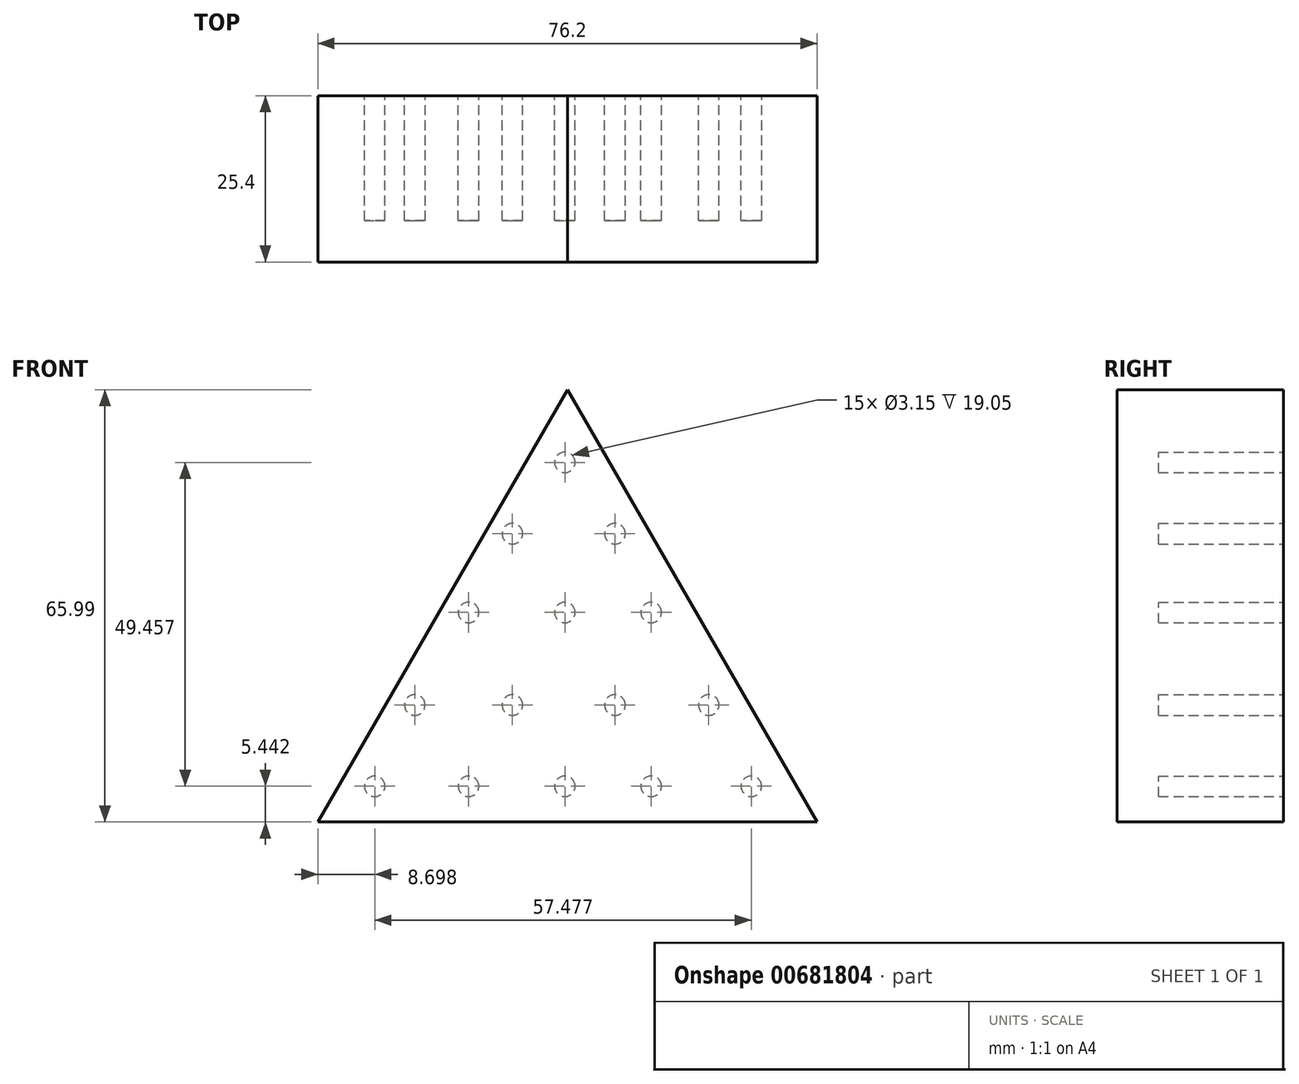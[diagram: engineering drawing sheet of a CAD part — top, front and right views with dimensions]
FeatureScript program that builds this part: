
annotation { "Feature Type Name" : "Feature", "Feature Type Description" : "" }
export const myFeature = defineFeature(function(context is Context, id is Id, definition is map)
    precondition{}
    {
        {
            var Q0;
            Q0=qCreatedBy(makeId("Front.planeOp"),FACE);
            var sketch = newSketch(context, id + "F0", { "sketchPlane" : qUnion([Q0])});
            skLineSegment(sketch, "E0", {"start": v(0, 0) * mm, "end": v(-38.1, 66) * mm});
            skLineSegment(sketch, "E1", {"start": v(-38.1, 66) * mm, "end": v(-76.2, 0) * mm});
            skLineSegment(sketch, "E2", {"start": v(-76.2, 0) * mm, "end": v(0, 0) * mm});
            skSolve(sketch);
        }
        {
            var Q0;
            Q0=makeQuery(id+"F0.imprint","IMPRINT",FACE,{"disambiguationData":[TD([[makeQuery(id+"F0.imprint","IMPRINT",EDGE,{"derivedFrom":sQuery(id+"F0.wireOp",EDGE,"E0")}),1.0]])]});
            extrude(context, id + "F1", {"entities" : qUnion([Q0]), "depth" : 25.4 * mm, "offsetDistance" : 25.4 * mm});
        }
        {
            var Q0;
            Q0=qCreatedBy(makeId("Front.planeOp"),FACE);
            var sketch = newSketch(context, id + "F2", { "sketchPlane" : qUnion([Q0])});
            skCircle(sketch, "E3", {"center": v(-38.48, 54.9) * mm, "radius": 1.57 * mm});
            skCircle(sketch, "E4", {"center": v(-46.5, 44.02) * mm, "radius": 1.57 * mm});
            skCircle(sketch, "E5", {"center": v(-53.18, 31.98) * mm, "radius": 1.57 * mm});
            skCircle(sketch, "E6", {"center": v(-61.4, 17.85) * mm, "radius": 1.57 * mm});
            skCircle(sketch, "E7", {"center": v(-67.5, 5.44) * mm, "radius": 1.57 * mm});
            skCircle(sketch, "E8", {"center": v(-30.84, 44.02) * mm, "radius": 1.57 * mm});
            skCircle(sketch, "E9", {"center": v(-38.48, 31.98) * mm, "radius": 1.57 * mm});
            skCircle(sketch, "E10", {"center": v(-25.3, 31.98) * mm, "radius": 1.57 * mm});
            skCircle(sketch, "E11", {"center": v(-46.5, 17.85) * mm, "radius": 1.57 * mm});
            skCircle(sketch, "E12", {"center": v(-30.84, 17.85) * mm, "radius": 1.57 * mm});
            skCircle(sketch, "E13", {"center": v(-16.52, 17.85) * mm, "radius": 1.57 * mm});
            skCircle(sketch, "E14", {"center": v(-38.48, 5.44) * mm, "radius": 1.57 * mm});
            skCircle(sketch, "E15", {"center": v(-53.18, 5.44) * mm, "radius": 1.57 * mm});
            skCircle(sketch, "E16", {"center": v(-25.3, 5.44) * mm, "radius": 1.57 * mm});
            skCircle(sketch, "E17", {"center": v(-10.03, 5.44) * mm, "radius": 1.57 * mm});
            skSolve(sketch);
        }
        {
            var Q0;
            Q0 = qSketchRegion(id + "F2", true);
            extrude(context, id + "F3", {"entities" : qUnion([Q0]), "operationType" : NewBodyOperationType.REMOVE, "depth" : 19.05 * mm, "offsetDistance" : 25.4 * mm});
        }
    });
